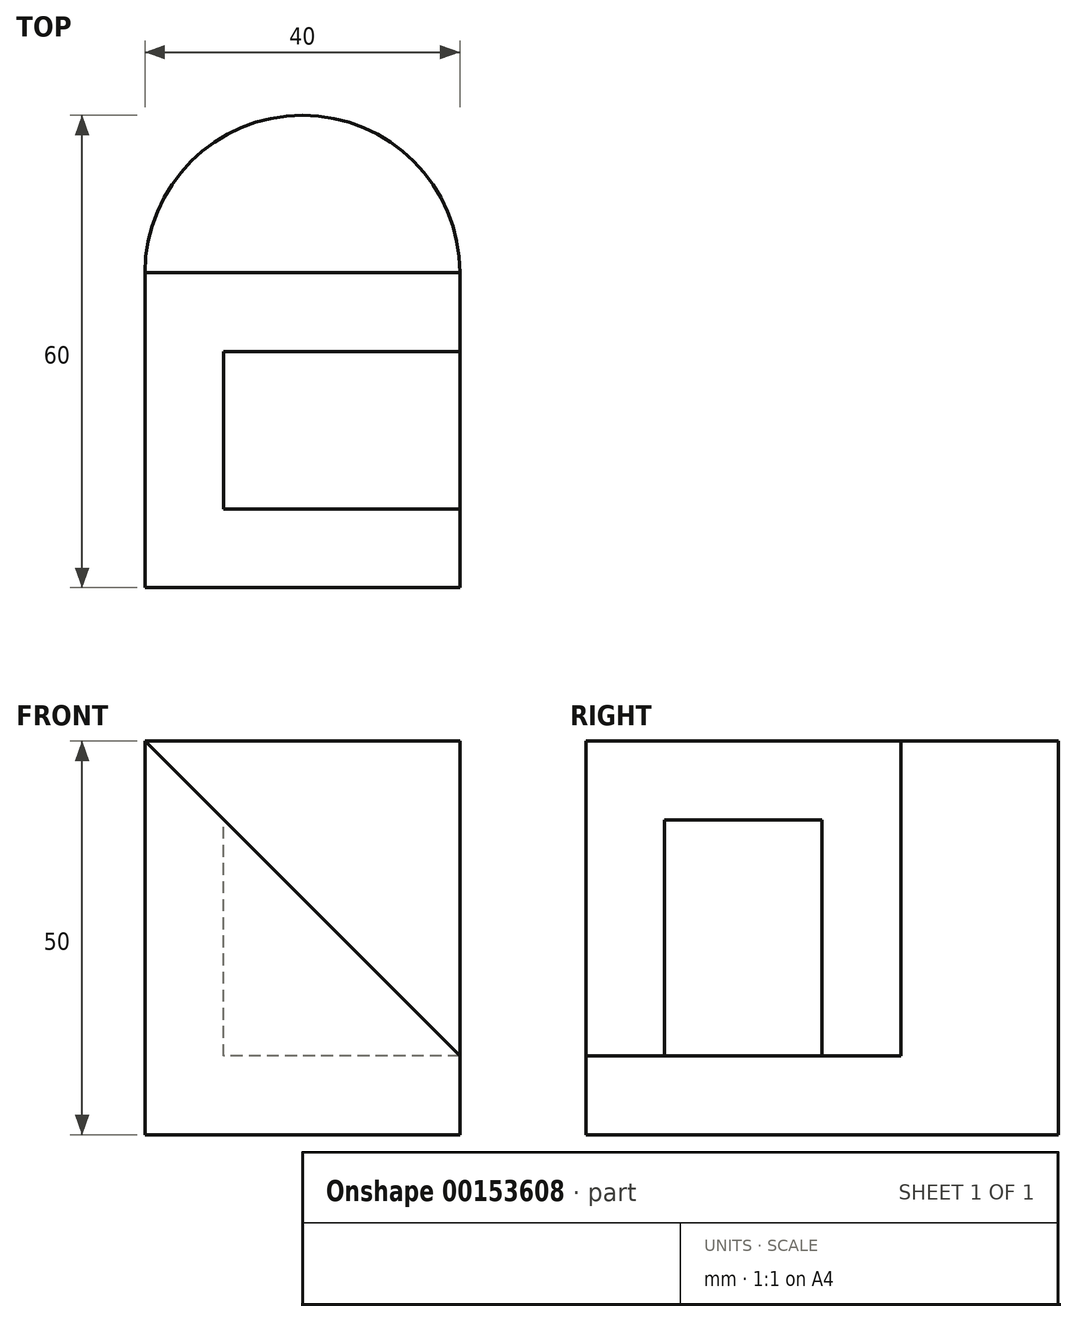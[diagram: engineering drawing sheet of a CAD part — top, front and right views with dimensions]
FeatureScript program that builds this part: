
annotation { "Feature Type Name" : "Feature", "Feature Type Description" : "" }
export const myFeature = defineFeature(function(context is Context, id is Id, definition is map)
    precondition{}
    {
        {
            var Q0;
            Q0=qCreatedBy(makeId("Top.planeOp"),FACE);
            var sketch = newSketch(context, id + "F0", { "sketchPlane" : qUnion([Q0])});
            skLineSegment(sketch, "E0.bottom", {"start": v(-20, 0) * mm, "end": v(20, 0) * mm});
            skLineSegment(sketch, "E0.left", {"start": v(-20, 0) * mm, "end": v(-20, 40) * mm});
            skLineSegment(sketch, "E0.right", {"start": v(20, 0) * mm, "end": v(20, 40) * mm});
            skArc(sketch, "E1", {"start": v(20, 40) * mm, "mid": v(0, 60) * mm, "end": v(-20, 40) * mm});
            skSolve(sketch);
        }
        {
            var Q0;
            Q0 = qSketchRegion(id + "F0", true);
            extrude(context, id + "F1", {"entities" : qUnion([Q0]), "depth" : 50 * mm});
        }
        {
            var Q0;
            Q0=makeQuery(id+"F1.opExtrude","SWEPT_FACE",FACE,{"disambiguationData":[OSD([sQuery(id+"F0.wireOp",EDGE,"E0.bottom")])]});
            var sketch = newSketch(context, id + "F2", { "sketchPlane" : qUnion([Q0])});
            skLineSegment(sketch, "E2", {"start": v(-20, 50) * mm, "end": v(20, 10) * mm});
            skLineSegment(sketch, "E3", {"start": v(20, 10) * mm, "end": v(20, 50) * mm});
            skLineSegment(sketch, "E4", {"start": v(20, 50) * mm, "end": v(-20, 50) * mm});
            skSolve(sketch);
        }
        {
            var Q0;
            Q0=makeQuery(id+"F1.opExtrude","CAP_FACE",FACE,{"disambiguationData":[OSD([sQuery(id+"F0.wireOp",EDGE,"E0.bottom"),sQuery(id+"F0.wireOp",EDGE,"E0.left"),sQuery(id+"F0.wireOp",EDGE,"E0.right"),sQuery(id+"F0.wireOp",EDGE,"E1")])],"isStart":false});
            var sketch = newSketch(context, id + "F3", { "sketchPlane" : qUnion([Q0])});
            skLineSegment(sketch, "E5.bottom", {"start": v(20, 10) * mm, "end": v(-10, 10) * mm});
            skLineSegment(sketch, "E5.top", {"start": v(20, 30) * mm, "end": v(-10, 30) * mm});
            skLineSegment(sketch, "E5.left", {"start": v(20, 10) * mm, "end": v(20, 30) * mm});
            skLineSegment(sketch, "E5.right", {"start": v(-10, 10) * mm, "end": v(-10, 30) * mm});
            skSolve(sketch);
        }
        {
            var Q0;
            Q0=makeQuery(id+"F3.imprint","IMPRINT",FACE,{"disambiguationData":[TD([[makeQuery(id+"F3.imprint","IMPRINT",EDGE,{"derivedFrom":sQuery(id+"F3.wireOp",EDGE,"E5.bottom")}),-1.0]])]});
            extrude(context, id + "F4", {"entities" : qUnion([Q0]), "operationType" : NewBodyOperationType.REMOVE, "oppositeDirection" : true, "depth" : 40 * mm});
        }
        {
            var Q0;
            Q0=makeQuery(id+"F2.imprint","IMPRINT",FACE,{"disambiguationData":[TD([[makeQuery(id+"F2.imprint","IMPRINT",EDGE,{"derivedFrom":sQuery(id+"F2.wireOp",EDGE,"E2")}),1.0]])]});
            extrude(context, id + "F5", {"entities" : qUnion([Q0]), "operationType" : NewBodyOperationType.REMOVE, "oppositeDirection" : true, "depth" : 40 * mm});
        }
    });
